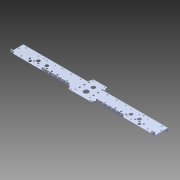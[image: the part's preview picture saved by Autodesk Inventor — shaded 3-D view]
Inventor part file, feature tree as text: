
AUTODESK INVENTOR PART (.ipt)
format: ipt  version: 2015 SP1 (Build 190203100, 203)  size: 511,488 bytes
history: native  units: in
note: dims shown in document units (in); Inventor stores cm internally (conversion verified against a paired STEP export)
features: reference x4, projected_geometry x3, other x2, extrude x2, sketch x2, chamfer x1, imported_body x1
ambient origin geometry x8: Origin, YZ Plane, XZ Plane, XY Plane, X Axis, Y Axis, Z Axis, Center Point
bodies: Body1 (feature_tree)
feature tree (15):
  other  "Cut-Extrude15"
  other  "AM14U2 Inside Sheet1"
  extrude  "Extrusion1"  Depth=6.25in
  extrude  "Extrusion2"  Depth=0.75in
  chamfer  "Chamfer1"  Distance=1.0in
  imported_body  "Base1"
  sketch  "Sketch1"  dims[d0=0.75in d1=6.25in]
  projected_geometry  "Projected Loop1"
  projected_geometry  "Projected Loop2"
  sketch  "Sketch2"  dims[d2=6.25in d3=0.75in d4=1.0in d5=0.0in d6=0.625in d7=0.625in d8=1.0in d9=0.0in d12=0.125in d13=0.125in d14=45.0deg]
  projected_geometry  "Projected Loop3"
  reference  "Reference1"
  reference  "Reference2"
  reference  "Reference3"
  reference  "Reference4"
